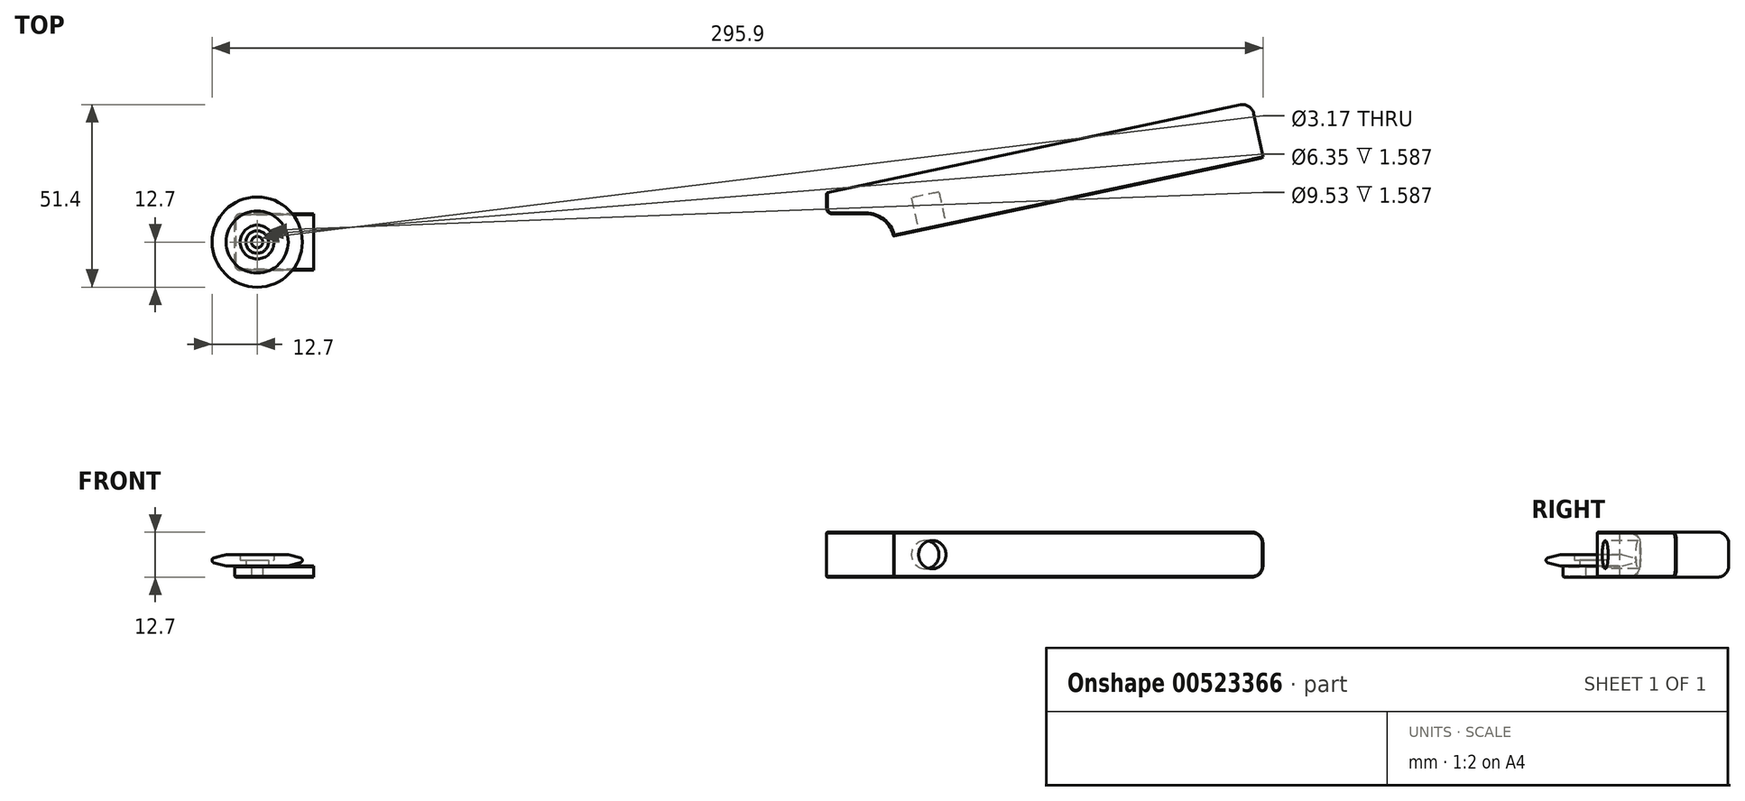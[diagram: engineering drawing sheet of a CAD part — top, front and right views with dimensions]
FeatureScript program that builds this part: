
annotation { "Feature Type Name" : "Feature", "Feature Type Description" : "" }
export const myFeature = defineFeature(function(context is Context, id is Id, definition is map)
    precondition{}
    {
        {
            var Q0;
            Q0=qCreatedBy(makeId("Top.planeOp"),FACE);
            var sketch = newSketch(context, id + "F0", { "sketchPlane" : qUnion([Q0])});
            skLineSegment(sketch, "E0.bottom", {"start": v(-177.8, 7.94) * mm, "end": v(0, 7.94) * mm});
            skLineSegment(sketch, "E0.top", {"start": v(-177.8, -7.94) * mm, "end": v(0, -7.94) * mm});
            skLineSegment(sketch, "E0.left", {"start": v(-177.8, 7.94) * mm, "end": v(-177.8, -7.94) * mm});
            skLineSegment(sketch, "E0.right", {"start": v(7.94, 7.94) * mm, "end": v(7.94, 1.69) * mm, "construction": true});
            skPoint(sketch, "E1", {"position": v(7.94, 0) * mm});
            skLineSegment(sketch, "E2", {"start": v(0, 0) * mm, "end": v(111.8, 23.76) * mm, "construction": true});
            skLineSegment(sketch, "E3", {"start": v(-39.01, 7.94) * mm, "end": v(-11.11, 13.87) * mm, "construction": true});
            skLineSegment(sketch, "E4", {"start": v(108.5, 39.3) * mm, "end": v(111.8, 23.76) * mm});
            skLineSegment(sketch, "E5", {"start": v(111.8, 23.76) * mm, "end": v(7.94, 1.69) * mm});
            skCircle(sketch, "E6", {"center": v(0, 0) * mm, "radius": 3.18 * mm});
            skLineSegment(sketch, "E7", {"start": v(5.9, 17.49) * mm, "end": v(9.2, 1.96) * mm, "construction": true});
            skLineSegment(sketch, "E8", {"start": v(7.94, 0) * mm, "end": v(-177.8, 0) * mm, "construction": true});
            skCircle(sketch, "E9", {"center": v(-171.45, 0) * mm, "radius": 1.59 * mm});
            skCircle(sketch, "E10", {"center": v(-171.45, 0) * mm, "radius": 12.7 * mm});
            skLineSegment(sketch, "E11", {"start": v(-155.58, 7.94) * mm, "end": v(-155.58, -7.94) * mm});
            skLineSegment(sketch, "E12", {"start": v(-11.11, 7.94) * mm, "end": v(-11.11, 13.87) * mm});
            skLineSegment(sketch, "E13", {"start": v(-11.11, 13.87) * mm, "end": v(-11.11, 13.87) * mm});
            skLineSegment(sketch, "E14", {"start": v(-11.11, 13.87) * mm, "end": v(108.5, 39.3) * mm});
            skArc(sketch, "E15", {"start": v(7.94, 0) * mm, "mid": v(5.61, -5.61) * mm, "end": v(0, -7.94) * mm});
            skLineSegment(sketch, "E16", {"start": v(0, -7.94) * mm, "end": v(7.94, -7.94) * mm, "construction": true});
            skLineSegment(sketch, "E17", {"start": v(7.94, 0) * mm, "end": v(7.94, -7.94) * mm, "construction": true});
            skLineSegment(sketch, "E18", {"start": v(0, 7.94) * mm, "end": v(0, 7.94) * mm});
            skLineSegment(sketch, "E19", {"start": v(7.94, 1.69) * mm, "end": v(7.76, 1.69) * mm});
            skArc(sketch, "E20", {"start": v(0, 7.94) * mm, "mid": v(4.98, 6.18) * mm, "end": v(7.76, 1.69) * mm});
            skLineSegment(sketch, "E21", {"start": v(0, 7.94) * mm, "end": v(7.94, 7.94) * mm, "construction": true});
            skLineSegment(sketch, "E22", {"start": v(7.94, 1.69) * mm, "end": v(7.94, 0) * mm});
            skLineSegment(sketch, "E23", {"start": v(-139.55, 53.08) * mm, "end": v(-53.85, 53.08) * mm, "construction": true});
            skSolve(sketch);
        }
        {
            var Q0;
            {var subQ1=sQuery(id+"F0.wireOp",EDGE,"E0.bottom");var subQ3=sQuery(id+"F0.wireOp",EDGE,"E3");var subQ4=makeQuery(id+"F0.imprint","INTERSECT",VERTEX,{"derivedFrom":[subQ1,subQ3]});Q0=makeQuery(id+"F0.imprint","IMPRINT",FACE,{"disambiguationData":[TD([[makeQuery(id+"F0.imprint","IMPRINT",EDGE,{"disambiguationData":[TD([[subQ4,-1.0]])],"derivedFrom":subQ3}),-1.0]])]});}
            var Q1;
            {var subQ1=sQuery(id+"F0.wireOp",EDGE,"E0.right");var subQ3=sQuery(id+"F0.wireOp",EDGE,"E5");var subQ4=makeQuery(id+"F0.imprint","INTERSECT",VERTEX,{"derivedFrom":[subQ1,subQ3]});Q1=makeQuery(id+"F0.imprint","IMPRINT",FACE,{"disambiguationData":[TD([[makeQuery(id+"F0.imprint","IMPRINT",EDGE,{"disambiguationData":[TD([[subQ4,1.0]])],"derivedFrom":subQ3}),-1.0]])]});}
            var Q2;
            {var subQ1=sQuery(id+"F0.wireOp",EDGE,"E4");Q2=makeQuery(id+"F0.imprint","IMPRINT",FACE,{"disambiguationData":[TD([[makeQuery(id+"F0.imprint","IMPRINT",EDGE,{"derivedFrom":subQ1}),-1.0]])]});}
            var Q3;
            Q3=makeQuery(id+"F0.imprint","IMPRINT",FACE,{"disambiguationData":[TD([[makeQuery(id+"F0.imprint","IMPRINT",EDGE,{"derivedFrom":sQuery(id+"F0.wireOp",EDGE,"E6")}),-1.0]])]});
            extrude(context, id + "F1", {"entities" : qUnion([Q0, Q1, Q2, Q3]), "depth" : 6.35 * mm, "offsetDistance" : 25.4 * mm});
        }
        {
            var Q0;
            {var subQ1=sQuery(id+"F0.wireOp",EDGE,"E4");Q0=makeQuery(id+"F0.imprint","IMPRINT",FACE,{"disambiguationData":[TD([[makeQuery(id+"F0.imprint","IMPRINT",EDGE,{"derivedFrom":subQ1}),-1.0]])]});}
            extrude(context, id + "F2", {"entities" : qUnion([Q0]), "operationType" : NewBodyOperationType.ADD, "depth" : 12.7 * mm, "offsetDistance" : 25.4 * mm});
        }
        {
            var Q0;
            {var subQ0=sQuery(id+"F0.wireOp",EDGE,"E0.left");Q0=makeQuery(id+"F0.imprint","IMPRINT",FACE,{"disambiguationData":[TD([[makeQuery(id+"F0.imprint","IMPRINT",EDGE,{"derivedFrom":subQ0}),1.0]])]});}
            var Q1;
            {var subQ0=sQuery(id+"F0.wireOp",EDGE,"E11");Q1=makeQuery(id+"F0.imprint","IMPRINT",FACE,{"disambiguationData":[TD([[makeQuery(id+"F0.imprint","IMPRINT",EDGE,{"derivedFrom":subQ0}),-1.0]])]});}
            extrude(context, id + "F3", {"entities" : qUnion([Q0, Q1]), "operationType" : NewBodyOperationType.ADD, "depth" : 3.17 * mm, "offsetDistance" : 25.4 * mm});
        }
        {
            var Q0;
            Q0=qCreatedBy(makeId("Front.planeOp"),FACE);
            var sketch = newSketch(context, id + "F4", { "sketchPlane" : qUnion([Q0])});
            skLineSegment(sketch, "E24", {"start": v(-171.45, 0) * mm, "end": v(-171.45, 59.25) * mm, "construction": true});
            skLineSegment(sketch, "E25.bottom", {"start": v(-184.15, 6.35) * mm, "end": v(-158.75, 6.35) * mm});
            skLineSegment(sketch, "E25.top", {"start": v(-184.15, 3.17) * mm, "end": v(-158.75, 3.17) * mm});
            skLineSegment(sketch, "E25.left", {"start": v(-184.15, 6.35) * mm, "end": v(-184.15, 3.17) * mm});
            skLineSegment(sketch, "E25.right", {"start": v(-158.75, 6.35) * mm, "end": v(-158.75, 3.17) * mm});
            skLineSegment(sketch, "E26", {"start": v(-180.19, 6.35) * mm, "end": v(-180.19, 3.17) * mm, "construction": true});
            skLineSegment(sketch, "E27", {"start": v(-180.19, 3.17) * mm, "end": v(-186.11, 4.76) * mm});
            skPoint(sketch, "E27.endSnap0", {"position": v(-184.15, 4.76) * mm});
            skLineSegment(sketch, "E28", {"start": v(-180.19, 6.35) * mm, "end": v(-186.11, 4.76) * mm});
            skLineSegment(sketch, "E29.bottom", {"start": v(-174.63, 6.35) * mm, "end": v(-168.28, 6.35) * mm});
            skLineSegment(sketch, "E29.top", {"start": v(-174.62, 3.17) * mm, "end": v(-168.28, 3.17) * mm});
            skLineSegment(sketch, "E29.left", {"start": v(-174.63, 6.35) * mm, "end": v(-174.63, 3.17) * mm});
            skLineSegment(sketch, "E29.right", {"start": v(-168.28, 6.35) * mm, "end": v(-168.28, 3.17) * mm});
            skLineSegment(sketch, "E30", {"start": v(-176.21, 6.35) * mm, "end": v(-176.21, 4.76) * mm});
            skLineSegment(sketch, "E31", {"start": v(-176.21, 4.76) * mm, "end": v(-174.63, 4.76) * mm});
            skSolve(sketch);
        }
        {
            var Q0;
            {var subQ11=sQuery(id+"F4.wireOp",EDGE,"E30");Q0=makeQuery(id+"F4.imprint","IMPRINT",FACE,{"disambiguationData":[TD([[makeQuery(id+"F4.imprint","IMPRINT",EDGE,{"derivedFrom":subQ11}),-1.0]])]});}
            var Q1;
            Q1=sQuery(id+"F4.wireOp",EDGE,"E24");
            revolve(context, id + "F5", {"entities" : qUnion([Q0]), "axis" : qUnion([Q1]), "revolveType" : RevolveType.FULL});
        }
        {
            var Q0;
            Q0=makeQuery(id+"F5.opRevolve","SWEPT_EDGE",EDGE,{"disambiguationData":[OSD([sQuery(id+"F4.wireOp",EDGE,"E25.left"),sQuery(id+"F4.wireOp",EDGE,"E27")])]});
            var Q1;
            Q1=makeQuery(id+"F5.opRevolve","SWEPT_EDGE",EDGE,{"disambiguationData":[OSD([sQuery(id+"F4.wireOp",EDGE,"E25.left"),sQuery(id+"F4.wireOp",EDGE,"E28")])]});
            fillet(context, id + "F6", {"entities" : qUnion([Q0, Q1]), "radius" : 0.64 * mm, "tangentPropagation" : true, "allowEdgeOverflow" : false});
        }
        {
            var Q0;
            Q0=makeQuery(id+"F3.opExtrude","SWEPT_EDGE",EDGE,{"disambiguationData":[OSD([sQuery(id+"F0.wireOp",EDGE,"E0.top"),sQuery(id+"F0.wireOp",EDGE,"E0.left")])]});
            var Q1;
            Q1=makeQuery(id+"F3.opExtrude","SWEPT_EDGE",EDGE,{"disambiguationData":[OSD([sQuery(id+"F0.wireOp",EDGE,"E0.bottom"),sQuery(id+"F0.wireOp",EDGE,"E0.left")])]});
            var Q2;
            Q2=makeQuery(id+"F1.opExtrude","SWEPT_EDGE",EDGE,{"disambiguationData":[OSD([sQuery(id+"F0.wireOp",EDGE,"E0.top"),sQuery(id+"F0.wireOp",EDGE,"E11")])]});
            var Q3;
            Q3=makeQuery(id+"F1.opExtrude","SWEPT_EDGE",EDGE,{"disambiguationData":[OSD([sQuery(id+"F0.wireOp",EDGE,"E0.bottom"),sQuery(id+"F0.wireOp",EDGE,"E11")])]});
            fillet(context, id + "F7", {"entities" : qUnion([Q0, Q1, Q2, Q3]), "radius" : 1.59 * mm, "tangentPropagation" : true, "allowEdgeOverflow" : false});
        }
        {
            var Q0;
            Q0=makeQuery(id+"F2.opExtrude","CAP_EDGE",EDGE,{"disambiguationData":[OSD([sQuery(id+"F0.wireOp",EDGE,"E14")])],"isStart":false});
            var Q1;
            Q1=makeQuery(id+"F1.opExtrude","CAP_EDGE",EDGE,{"disambiguationData":[OSD([sQuery(id+"F0.wireOp",EDGE,"E14")])],"isStart":true});
            var Q2;
            Q2=makeQuery(id+"F2.opExtrude","CAP_EDGE",EDGE,{"disambiguationData":[OSD([sQuery(id+"F0.wireOp",EDGE,"E4")])],"isStart":false});
            var Q3;
            Q3=makeQuery(id+"F1.opExtrude","CAP_EDGE",EDGE,{"disambiguationData":[OSD([sQuery(id+"F0.wireOp",EDGE,"E4")])],"isStart":true});
            var Q4;
            {var subQ0=sQuery(id+"F0.wireOp",EDGE,"E14");var subQ1=sQuery(id+"F0.wireOp",EDGE,"E4");Q4=makeQuery(id+"F2.boolean.opBoolean","MERGE",EDGE,{"derivedFrom":[makeQuery(id+"F1.opExtrude","SWEPT_EDGE",EDGE,{"disambiguationData":[OSD([subQ1,subQ0])]}),makeQuery(id+"F2.opExtrude","SWEPT_EDGE",EDGE,{"disambiguationData":[OSD([subQ1,subQ0])]})]});}
            fillet(context, id + "F8", {"entities" : qUnion([Q0, Q1, Q2, Q3, Q4]), "radius" : 3.17 * mm, "tangentPropagation" : true, "allowEdgeOverflow" : false});
        }
        {
            var Q0;
            {var subQ0=sQuery(id+"F0.wireOp",EDGE,"E5");Q0=makeQuery(id+"F2.boolean.opBoolean","MERGE",FACE,{"derivedFrom":[makeQuery(id+"F1.opExtrude","SWEPT_FACE",FACE,{"disambiguationData":[OSD([subQ0])]}),makeQuery(id+"F2.opExtrude","SWEPT_FACE",FACE,{"disambiguationData":[OSD([subQ0])]})]});}
            cPlane(context, id + "F9", {"entities" : qUnion([Q0]), "cplaneType" : CPlaneType.OFFSET, "offset" : 0 * mm, "width" : 152.4 * mm, "height" : 152.4 * mm});
        }
        {
            var Q0;
            Q0=qCreatedBy(id+"F9.planeOp",FACE);
            var sketch = newSketch(context, id + "F10", { "sketchPlane" : qUnion([Q0])});
            skLineSegment(sketch, "E32", {"start": v(125.09, 6.35) * mm, "end": v(9.63, 6.35) * mm, "construction": true});
            skCircle(sketch, "E33", {"center": v(19.05, 6.35) * mm, "radius": 3.97 * mm});
            skSolve(sketch);
        }
        {
            var Q0;
            Q0=makeQuery(id+"F10.imprint","IMPRINT",FACE,{"disambiguationData":[TD([[makeQuery(id+"F10.imprint","IMPRINT",EDGE,{"derivedFrom":sQuery(id+"F10.wireOp",EDGE,"E33")}),1.0]])]});
            extrude(context, id + "F11", {"entities" : qUnion([Q0]), "operationType" : NewBodyOperationType.REMOVE, "oppositeDirection" : true, "depth" : 9.52 * mm, "offsetDistance" : 25.4 * mm});
        }
        {
            var Q0;
            Q0=makeQuery(id+"F1.opExtrude","CAP_EDGE",EDGE,{"disambiguationData":[OSD([sQuery(id+"F0.wireOp",EDGE,"E0.bottom")])],"isStart":false});
            var Q1;
            {var subQ0=sQuery(id+"F0.wireOp",EDGE,"E0.bottom");Q1=makeQuery(id+"F3.boolean.opBoolean","MERGE",EDGE,{"derivedFrom":[makeQuery(id+"F1.opExtrude","CAP_EDGE",EDGE,{"disambiguationData":[OSD([subQ0])],"isStart":true}),makeQuery(id+"F3.opExtrude","CAP_EDGE",EDGE,{"disambiguationData":[OSD([subQ0])],"isStart":true})]});}
            var Q2;
            Q2=makeQuery(id+"F1.opExtrude","CAP_EDGE",EDGE,{"disambiguationData":[OSD([sQuery(id+"F0.wireOp",EDGE,"E5")])],"isStart":true});
            var Q3;
            Q3=makeQuery(id+"F2.opExtrude","CAP_EDGE",EDGE,{"disambiguationData":[OSD([sQuery(id+"F0.wireOp",EDGE,"E20")])],"isStart":false});
            var Q4;
            Q4=makeQuery(id+"F2.opExtrude","CAP_EDGE",EDGE,{"disambiguationData":[OSD([sQuery(id+"F0.wireOp",EDGE,"E12")])],"isStart":false});
            var Q5;
            Q5=makeQuery(id+"F11.boolean.opBoolean","COPY",EDGE,{"derivedFrom":makeQuery(id+"F11.opExtrude","CAP_EDGE",EDGE,{"disambiguationData":[OSD([sQuery(id+"F10.wireOp",EDGE,"E33")])],"isStart":true})});
            var Q6;
            Q6=makeQuery(id+"F3.opExtrude","CAP_EDGE",EDGE,{"disambiguationData":[OSD([sQuery(id+"F0.wireOp",EDGE,"E0.top")])],"isStart":false});
            chamfer(context, id + "F12", {"entities" : qUnion([Q0, Q1, Q2, Q3, Q4, Q5, Q6]), "width" : 0.25 * mm, "tangentPropagation" : true});
        }
    });
